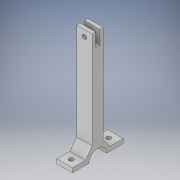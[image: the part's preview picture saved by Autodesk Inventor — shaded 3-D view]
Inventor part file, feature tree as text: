
AUTODESK INVENTOR PART (.ipt)
format: ipt  version: 2019 (Build 230136000, 136)  size: 174,080 bytes
history: native  units: mm
features: extrude x6, sketch x6
ambient origin geometry x8: Origin, YZ Plane, XZ Plane, XY Plane, X Axis, Y Axis, Z Axis, Center Point
bodies: Solid1 (feature_tree)
feature tree (12):
  extrude  "Extrusion1"  Depth=7.0mm
  extrude  "Extrusion2"  Depth=1.5mm
  extrude  "Extrusion3"  Depth=6.0mm TaperAngle=0.0deg
  extrude  "Extrusion4"  Depth=2.0mm
  extrude  "Extrusion5"  Depth=6.0mm TaperAngle=0.0deg
  extrude  "Extrusion6"  Depth=6.0mm TaperAngle=0.0deg
  sketch  "Sketch1"  dims[d0=5.0mm d1=7.0mm]
  sketch  "Sketch2"  dims[d2=50.0mm d3=0.0mm d4=1.5mm]
  sketch  "Sketch3"  dims[d5=1.5mm d6=6.0mm d7=0.0mm]
  sketch  "Sketch4"  dims[d8=2.0mm d9=3.0mm]
  sketch  "Sketch6"  dims[d10=3.5mm d11=6.0mm d12=0.0mm]
  sketch  "Sketch7"  dims[d21=8.0mm d22=6.0mm d23=0.0mm d26=3.0mm d27=3.0mm d28=8.0mm d29=2.0mm d30=7.0mm d31=0.0mm d32=2.0mm d33=3.0mm d34=3.5mm d35=3.5mm d36=3.0mm d37=2.0mm d38=7.0mm d39=0.0mm]
